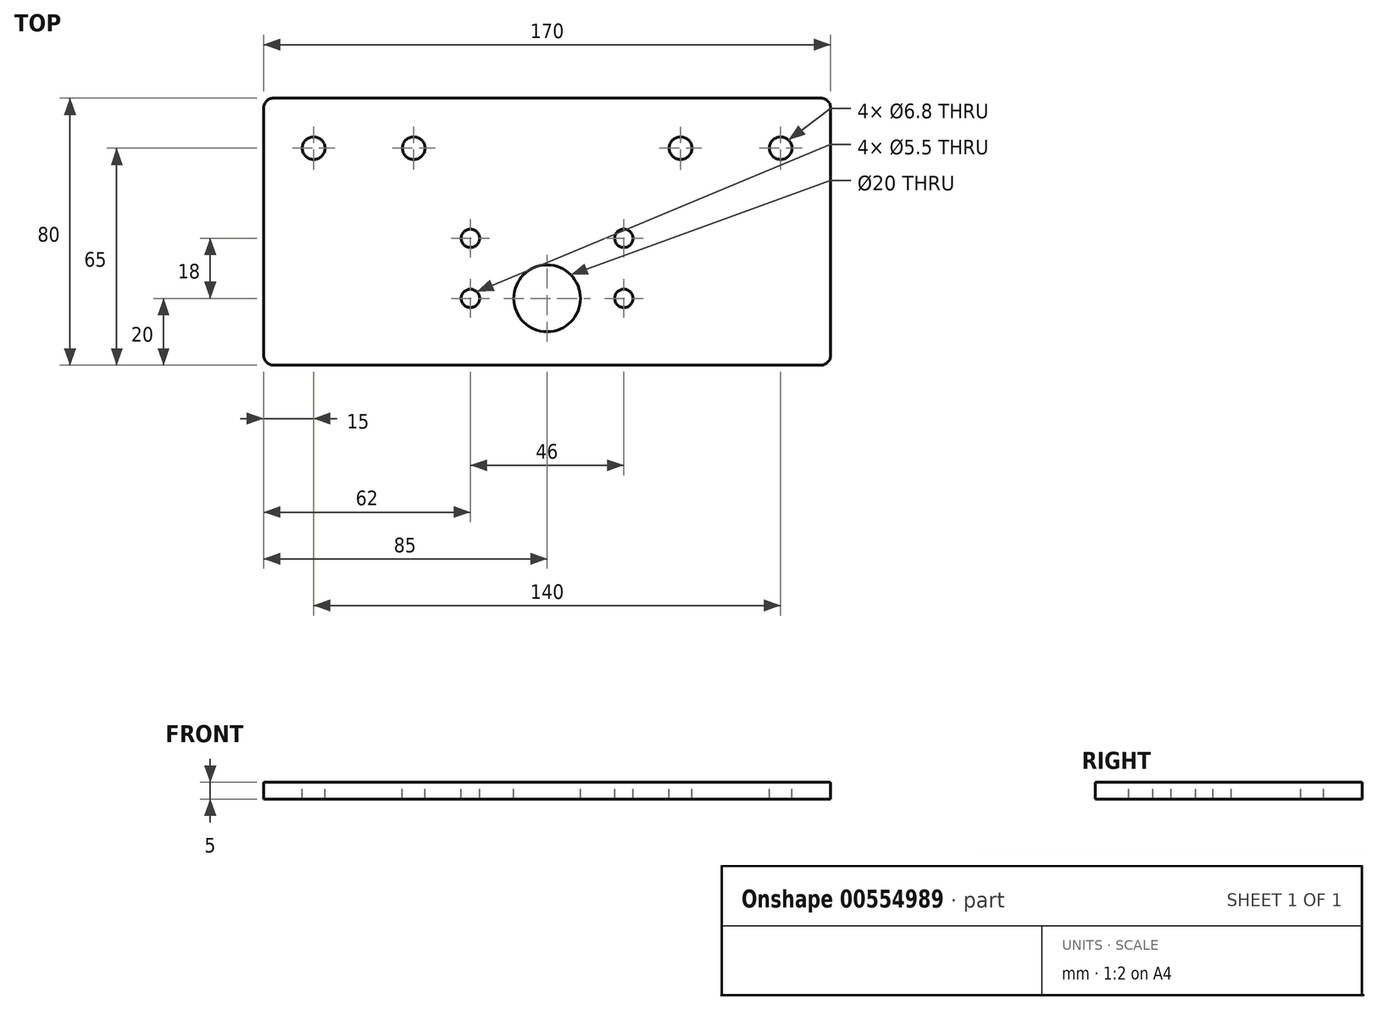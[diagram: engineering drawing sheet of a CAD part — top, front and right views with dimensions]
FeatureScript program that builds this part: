
annotation { "Feature Type Name" : "Feature", "Feature Type Description" : "" }
export const myFeature = defineFeature(function(context is Context, id is Id, definition is map)
    precondition{}
    {
        {
            var Q0;
            Q0=qCreatedBy(makeId("Top.planeOp"),FACE);
            var sketch = newSketch(context, id + "F0", { "sketchPlane" : qUnion([Q0])});
            skLineSegment(sketch, "E0.bottom", {"start": v(85, 40) * mm, "end": v(-85, 40) * mm});
            skLineSegment(sketch, "E0.top", {"start": v(85, -40) * mm, "end": v(-85, -40) * mm});
            skLineSegment(sketch, "E0.left", {"start": v(85, 40) * mm, "end": v(85, -40) * mm});
            skLineSegment(sketch, "E0.right", {"start": v(-85, 40) * mm, "end": v(-85, -40) * mm});
            skPoint(sketch, "E0.middle", {"position": v(0, 0) * mm});
            skSolve(sketch);
        }
        {
            var Q0;
            Q0=qSketchRegion(id+"F0",true);
            extrude(context, id + "F1", {"entities" : qUnion([Q0]), "endBound" : BoundingType.SYMMETRIC, "depth" : 5 * mm, "offsetDistance" : 25 * mm});
        }
        {
            var Q0;
            Q0=makeQuery(id+"F1.opExtrude","CAP_FACE",FACE,{"disambiguationData":[OSD([sQuery(id+"F0.wireOp",EDGE,"E0.bottom"),sQuery(id+"F0.wireOp",EDGE,"E0.top"),sQuery(id+"F0.wireOp",EDGE,"E0.left"),sQuery(id+"F0.wireOp",EDGE,"E0.right")])],"isStart":false});
            var sketch = newSketch(context, id + "F2", { "sketchPlane" : qUnion([Q0])});
            skCircle(sketch, "E1", {"center": v(40, 25) * mm, "radius": 3.4 * mm});
            skCircle(sketch, "E2", {"center": v(70, 25) * mm, "radius": 3.4 * mm});
            skCircle(sketch, "E3.MirrorC", {"center": v(-40, 25) * mm, "radius": 3.4 * mm});
            skCircle(sketch, "E4.MirrorC", {"center": v(-70, 25) * mm, "radius": 3.4 * mm});
            skCircle(sketch, "E5", {"center": v(0, -20) * mm, "radius": 10 * mm});
            skCircle(sketch, "E6", {"center": v(-23, -2) * mm, "radius": 2.75 * mm});
            skCircle(sketch, "E7", {"center": v(-23, -20) * mm, "radius": 2.75 * mm});
            skCircle(sketch, "E8", {"center": v(23, -2) * mm, "radius": 2.75 * mm});
            skCircle(sketch, "E9", {"center": v(23, -20) * mm, "radius": 2.75 * mm});
            skSolve(sketch);
        }
        {
            var Q0;
            Q0=qSketchRegion(id+"F2",true);
            extrude(context, id + "F3", {"entities" : qUnion([Q0]), "operationType" : NewBodyOperationType.REMOVE, "oppositeDirection" : true, "depth" : 5 * mm, "offsetDistance" : 25 * mm});
        }
        {
            var Q0;
            Q0=makeQuery(id+"F1.opExtrude","SWEPT_EDGE",EDGE,{"disambiguationData":[OSD([sQuery(id+"F0.wireOp",EDGE,"E0.top"),sQuery(id+"F0.wireOp",EDGE,"E0.right")])]});
            var Q1;
            Q1=makeQuery(id+"F1.opExtrude","SWEPT_EDGE",EDGE,{"disambiguationData":[OSD([sQuery(id+"F0.wireOp",EDGE,"E0.top"),sQuery(id+"F0.wireOp",EDGE,"E0.left")])]});
            var Q2;
            Q2=makeQuery(id+"F1.opExtrude","SWEPT_EDGE",EDGE,{"disambiguationData":[OSD([sQuery(id+"F0.wireOp",EDGE,"E0.bottom"),sQuery(id+"F0.wireOp",EDGE,"E0.right")])]});
            var Q3;
            Q3=makeQuery(id+"F1.opExtrude","SWEPT_EDGE",EDGE,{"disambiguationData":[OSD([sQuery(id+"F0.wireOp",EDGE,"E0.bottom"),sQuery(id+"F0.wireOp",EDGE,"E0.left")])]});
            fillet(context, id + "F4", {"entities" : qUnion([Q0, Q1, Q2, Q3]), "radius" : 3 * mm, "tangentPropagation" : true, "allowEdgeOverflow" : false});
        }
    });
